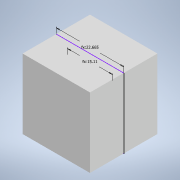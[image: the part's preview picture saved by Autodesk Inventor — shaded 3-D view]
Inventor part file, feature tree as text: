
AUTODESK INVENTOR PART (.ipt)
format: ipt  version: 2022 (Build 260153000, 153)  size: 131,584 bytes
history: native  units: mm
features: other x2, extrude x2, sketch x1
ambient origin geometry x8: Origin, YZ Plane, XZ Plane, XY Plane, X Axis, Y Axis, Z Axis, Center Point
bodies: Body1 (feature_tree)
feature tree (5):
  other  "Těleso1"
  sketch  "Náčrt1"
  extrude  "Vysunutí1"  Depth=15.110215mm
  extrude  "Vysunutí2"  Depth=22.665322mm
  other  "Rotace1"
